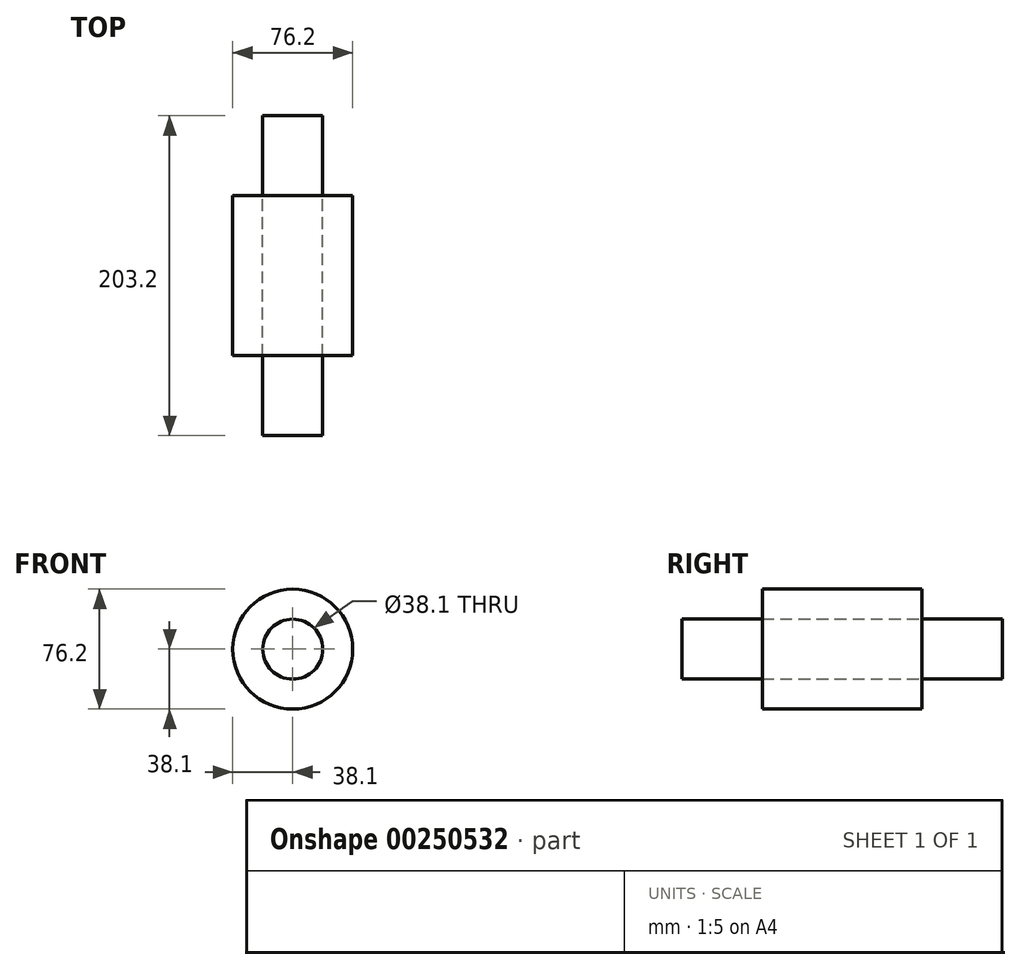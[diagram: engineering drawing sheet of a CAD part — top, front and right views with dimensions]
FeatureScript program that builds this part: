
annotation { "Feature Type Name" : "Feature", "Feature Type Description" : "" }
export const myFeature = defineFeature(function(context is Context, id is Id, definition is map)
    precondition{}
    {
        {
            var Q0;
            Q0=qCreatedBy(makeId("Front.planeOp"),FACE);
            var sketch = newSketch(context, id + "F0", { "sketchPlane" : qUnion([Q0])});
            skCircle(sketch, "E0", {"center": v(0, 0) * mm, "radius": 38.1 * mm});
            skCircle(sketch, "E1", {"center": v(0, 0) * mm, "radius": 19.05 * mm});
            skSolve(sketch);
        }
        {
            var Q0;
            Q0 = qSketchRegion(id + "F0", true);
            extrude(context, id + "F1", {"entities" : qUnion([Q0]), "endBound" : BoundingType.SYMMETRIC, "depth" : 101.6 * mm});
        }
        {
            var Q0;
            Q0=makeQuery(id+"F0.imprint","IMPRINT",FACE,{"disambiguationData":[TD([[makeQuery(id+"F0.imprint","IMPRINT",EDGE,{"derivedFrom":sQuery(id+"F0.wireOp",EDGE,"E1")}),1.0]])]});
            var Q1;
            Q1=sQuery(id+"F0.wireOp",EDGE,"E1");
            extrude(context, id + "F2", {"entities" : qUnion([Q0]), "surfaceEntities" : qUnion([Q1]), "endBound" : BoundingType.SYMMETRIC, "depth" : 203.2 * mm});
        }
    });
